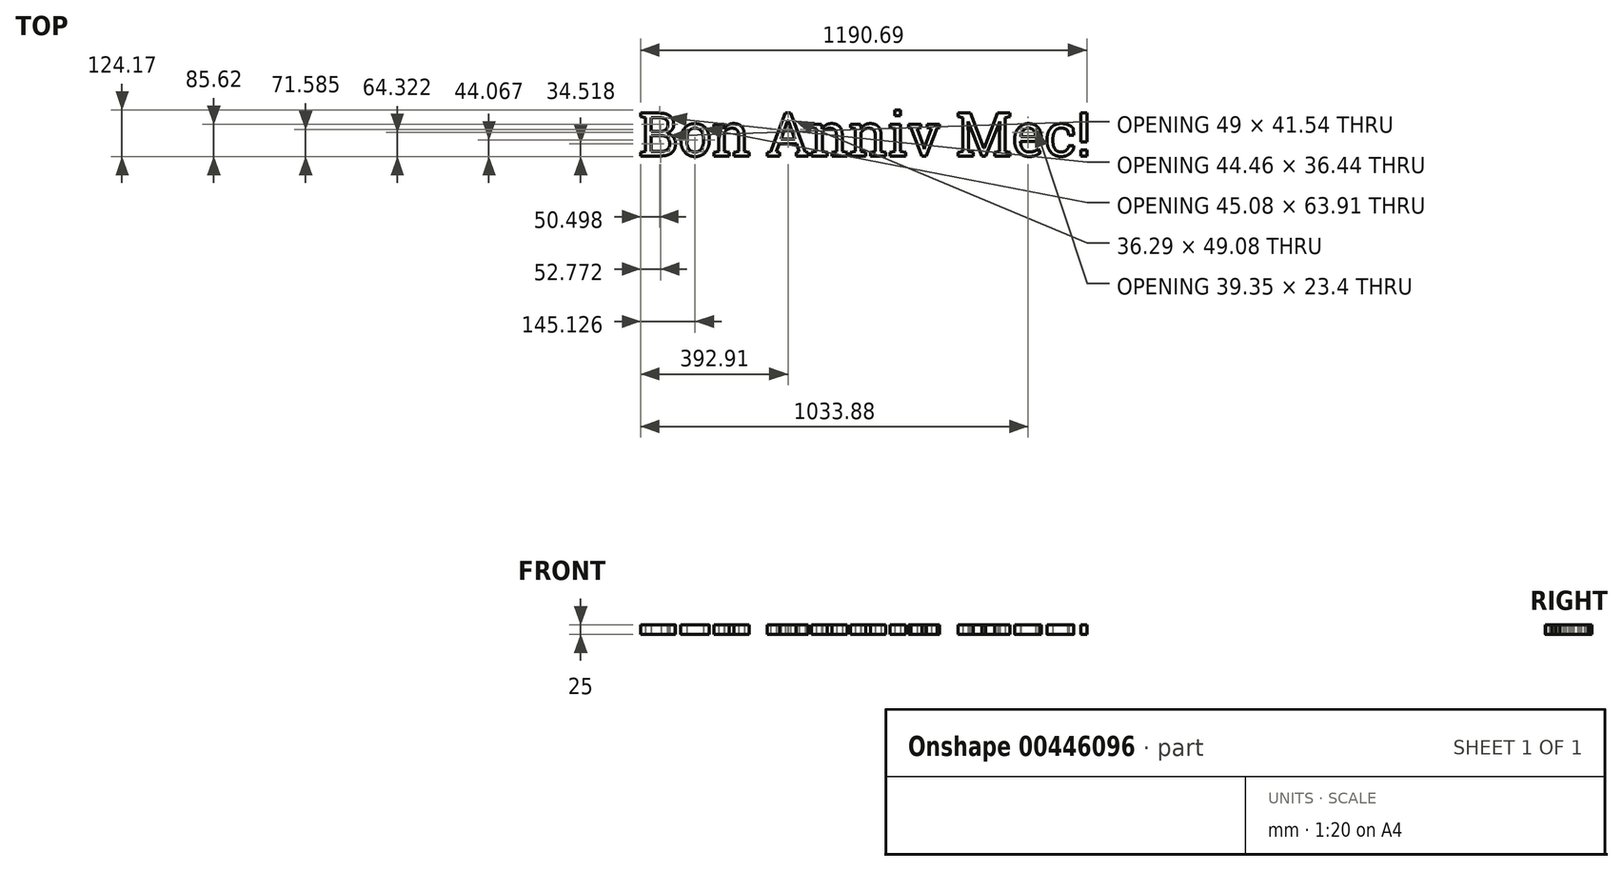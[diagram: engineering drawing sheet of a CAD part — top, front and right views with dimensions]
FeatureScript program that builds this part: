
annotation { "Feature Type Name" : "Feature", "Feature Type Description" : "" }
export const myFeature = defineFeature(function(context is Context, id is Id, definition is map)
    precondition{}
    {
        {
            var Q0;
            Q0=qCreatedBy(makeId("Top.planeOp"),FACE);
            var sketch = newSketch(context, id + "F0", { "sketchPlane" : qUnion([Q0])});
            skText(sketch, "E0", { "text": "Bon Anniv Mec!", "fontName": "RobotoSlab-Regular.ttf"});
            const initialGuessF0  = {"E0": [-0.14166, -0.052, 1, 0, 0.1158]};
            skSetInitialGuess(sketch, initialGuessF0);
            skSolve(sketch);
        }
        {
            var Q0;
            Q0 = qSketchRegion(id + "F0", true);
            extrude(context, id + "F1", {"entities" : qUnion([Q0]), "depth" : 25 * mm});
        }
    });
